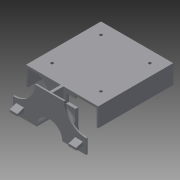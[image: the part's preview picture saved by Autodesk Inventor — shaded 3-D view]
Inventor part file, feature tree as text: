
AUTODESK INVENTOR PART (.ipt)
format: ipt  version: 2014 SP2 (Build 180247200, 247)  size: 279,040 bytes
history: native  units: mm
features: extrude x8, sketch x8, fillet x4, chamfer x2, other x1, projected_geometry x1
ambient origin geometry x8: Origin, YZ Plane, XZ Plane, XY Plane, X Axis, Y Axis, Z Axis, Center Point
bodies: Body1 (feature_tree)
feature tree (24):
  other  "ソリッド1"
  extrude  "押し出し1"  Depth=1.5mm
  extrude  "押し出し2"  Depth=23.0mm
  extrude  "押し出し3"  Depth=12.5mm TaperAngle=0.0deg
  fillet  "フィレット1"  Radius=30.0mm
  extrude  "押し出し4"  Depth=2.5mm TaperAngle=0.0deg
  extrude  "押し出し5"  Depth=65.0mm
  fillet  "フィレット2"  [1 undecoded]
  extrude  "押し出し6"  Depth=65.0mm
  fillet  "フィレット4"  Radius=32.5mm
  extrude  "押し出し7"  Depth=2.0mm TaperAngle=0.0deg
  chamfer  "面取り1"  Distance=2.5mm
  chamfer  "面取り2"  Distance=2.5mm
  fillet  "フィレット5"  Radius=2.5mm
  extrude  "押し出し8"  Depth=2.5mm
  sketch  "スケッチ1"
  sketch  "スケッチ2"
  sketch  "スケッチ3"
  sketch  "スケッチ5"
  sketch  "スケッチ6"
  sketch  "スケッチ7"
  sketch  "スケッチ8"
  sketch  "スケッチ9"
  projected_geometry  "投影ループ1"
note: 1 required parameter value undecoded (feature->parameter linkage not recoverable at this tier; creation-order binding heuristic only, values carry confidence <= 0.55)
